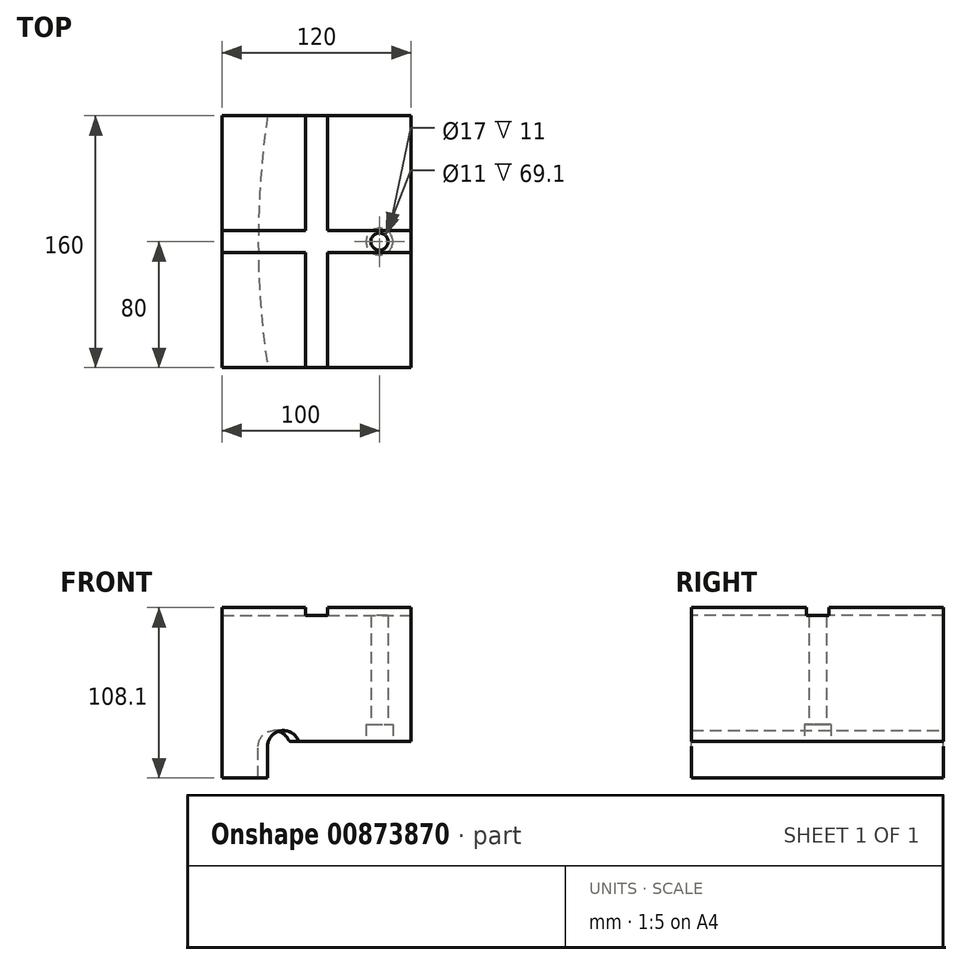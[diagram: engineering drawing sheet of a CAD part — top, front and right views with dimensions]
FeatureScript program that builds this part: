
annotation { "Feature Type Name" : "Feature", "Feature Type Description" : "" }
export const myFeature = defineFeature(function(context is Context, id is Id, definition is map)
    precondition{}
    {
        {
            var Q0;
            Q0=qCreatedBy(makeId("Front.planeOp"),FACE);
            var sketch = newSketch(context, id + "F0", { "sketchPlane" : qUnion([Q0])});
            skLineSegment(sketch, "E0", {"start": v(-542, 114.4) * mm, "end": v(-542, 136.4) * mm});
            skArc(sketch, "E1", {"start": v(-523.02, 140.8) * mm, "mid": v(-534.26, 146.14) * mm, "end": v(-542, 136.4) * mm});
            skLineSegment(sketch, "E2", {"start": v(-445, 139.4) * mm, "end": v(-520.78, 139.4) * mm});
            skPoint(sketch, "E3.visualSharp", {"position": v(-522.46, 139.4) * mm});
            skArc(sketch, "E3.filletArc", {"start": v(-523.02, 140.8) * mm, "mid": v(-522.1, 139.78) * mm, "end": v(-520.78, 139.4) * mm});
            skLineSegment(sketch, "E4", {"start": v(-542, 116.4) * mm, "end": v(-542, 114.4) * mm, "construction": true});
            skLineSegment(sketch, "E5", {"start": v(-445, 139.4) * mm, "end": v(-445, 224.5) * mm});
            skLineSegment(sketch, "E6", {"start": v(-445, 224.5) * mm, "end": v(-565, 224.5) * mm});
            skLineSegment(sketch, "E7", {"start": v(-565, 224.5) * mm, "end": v(-565, 116.4) * mm});
            skLineSegment(sketch, "E8", {"start": v(-565, 116.4) * mm, "end": v(-542, 116.4) * mm});
            skSolve(sketch);
        }
        {
            var Q0;
            Q0=qCreatedBy(makeId("Top.planeOp"),FACE);
            cPlane(context, id + "F1", {"entities" : qUnion([Q0]), "cplaneType" : CPlaneType.OFFSET, "offset" : 139.4 * mm, "width" : 150 * mm, "height" : 150 * mm});
        }
        {
            var Q0;
            Q0=qCreatedBy(id+"F1.planeOp",FACE);
            var sketch = newSketch(context, id + "F2", { "sketchPlane" : qUnion([Q0])});
            skArc(sketch, "E9", {"start": v(-340.89, 286.04) * mm, "mid": v(-445, 0) * mm, "end": v(-340.89, -286.04) * mm});
            skLineSegment(sketch, "E10", {"start": v(0, 0) * mm, "end": v(-340.89, 286.04) * mm, "construction": true});
            skLineSegment(sketch, "E11.MirrorCS", {"start": v(0, 0) * mm, "end": v(-340.89, -286.04) * mm, "construction": true});
            skSolve(sketch);
        }
        {
            var Q0;
            {var subQ0=sQuery(id+"F0.wireOp",EDGE,"E1");Q0=makeQuery(id+"F0.imprint","IMPRINT",FACE,{"disambiguationData":[TD([[makeQuery(id+"F0.imprint","IMPRINT",EDGE,{"derivedFrom":subQ0}),-1.0]])]});}
            var Q1;
            Q1=sQuery(id+"F2.wireOp",EDGE,"E9");
            sweep(context, id + "F3", {"profiles" : qUnion([Q0]), "path" : qUnion([Q1])});
        }
        {
            var Q0;
            Q0=makeQuery(id+"F3.opSweep","SWEPT_FACE",FACE,{"disambiguationData":[OSD([sQuery(id+"F0.wireOp",EDGE,"E6"),sQuery(id+"F2.wireOp",EDGE,"E9")])]});
            var sketch = newSketch(context, id + "F4", { "sketchPlane" : qUnion([Q0])});
            skLineSegment(sketch, "E12.bottom", {"start": v(-559.3, 80) * mm, "end": v(-445, 80) * mm});
            skLineSegment(sketch, "E12.top", {"start": v(-559.3, -80) * mm, "end": v(-445, -80) * mm});
            skLineSegment(sketch, "E12.right", {"start": v(-445, 80) * mm, "end": v(-445, -80) * mm});
            skLineSegment(sketch, "E13", {"start": v(0, 0) * mm, "end": v(-445, 0) * mm, "construction": true});
            skArc(sketch, "E14", {"start": v(-432.82, 363.17) * mm, "mid": v(-565, 0) * mm, "end": v(-432.82, -363.17) * mm});
            skArc(sketch, "E15", {"start": v(-340.89, 286.04) * mm, "mid": v(-445, 0) * mm, "end": v(-340.89, -286.04) * mm});
            skLineSegment(sketch, "E16", {"start": v(-432.82, 363.17) * mm, "end": v(0, 0) * mm, "construction": true});
            skLineSegment(sketch, "E17", {"start": v(-432.82, -363.17) * mm, "end": v(0, 0) * mm, "construction": true});
            skLineSegment(sketch, "E18", {"start": v(-432.82, -363.17) * mm, "end": v(-340.89, -286.04) * mm});
            skLineSegment(sketch, "E19", {"start": v(-432.82, 363.17) * mm, "end": v(-340.89, 286.04) * mm});
            skSolve(sketch);
        }
        {
            var Q0;
            {var subQ2=sQuery(id+"F4.wireOp",EDGE,"E12.bottom");Q0=makeQuery(id+"F4.imprint","IMPRINT",FACE,{"disambiguationData":[TD([[makeQuery(id+"F4.imprint","IMPRINT",EDGE,{"derivedFrom":subQ2}),1.0]])]});}
            var Q1;
            {var subQ4=sQuery(id+"F4.wireOp",EDGE,"E12.top");Q1=makeQuery(id+"F4.imprint","IMPRINT",FACE,{"disambiguationData":[TD([[makeQuery(id+"F4.imprint","IMPRINT",EDGE,{"derivedFrom":subQ4}),-1.0]])]});}
            extrude(context, id + "F5", {"entities" : qUnion([Q0, Q1]), "operationType" : NewBodyOperationType.REMOVE, "endBound" : BoundingType.UP_TO_NEXT, "oppositeDirection" : true, "depth" : 25 * mm, "offsetDistance" : 25 * mm});
        }
        {
            var Q0;
            Q0=makeQuery(id+"F3.opSweep","SWEPT_FACE",FACE,{"disambiguationData":[OSD([sQuery(id+"F0.wireOp",EDGE,"E6"),sQuery(id+"F2.wireOp",EDGE,"E9")])]});
            var sketch = newSketch(context, id + "F6", { "sketchPlane" : qUnion([Q0])});
            skLineSegment(sketch, "E20", {"start": v(-559.3, 80) * mm, "end": v(-565, 80) * mm});
            skLineSegment(sketch, "E21", {"start": v(-565, 80) * mm, "end": v(-565, -80) * mm});
            skLineSegment(sketch, "E22", {"start": v(-565, -80) * mm, "end": v(-559.3, -80) * mm});
            skArc(sketch, "E23", {"start": v(-559.3, 80) * mm, "mid": v(-565, 0) * mm, "end": v(-559.3, -80) * mm});
            skSolve(sketch);
        }
        {
            var Q0;
            Q0 = qSketchRegion(id + "F6", true);
            var Q1;
            Q1=makeQuery(id+"F3.opSweep","SWEPT_FACE",FACE,{"disambiguationData":[OSD([sQuery(id+"F0.wireOp",EDGE,"E8"),sQuery(id+"F2.wireOp",EDGE,"E9")])]});
            extrude(context, id + "F7", {"entities" : qUnion([Q0]), "operationType" : NewBodyOperationType.ADD, "endBound" : BoundingType.UP_TO_SURFACE, "oppositeDirection" : true, "depth" : 25 * mm, "endBoundEntityFace" : qUnion([Q1]), "offsetDistance" : 25 * mm});
        }
        {
            var Q0;
            {var subQ0=sQuery(id+"F6.wireOp",EDGE,"E23");var subQ1=sQuery(id+"F6.wireOp",EDGE,"E21");Q0=makeQuery(id+"F7.boolean.opBoolean","MERGE",FACE,{"derivedFrom":[makeQuery(id+"F3.opSweep","SWEPT_FACE",FACE,{"disambiguationData":[OSD([sQuery(id+"F0.wireOp",EDGE,"E6"),sQuery(id+"F2.wireOp",EDGE,"E9")])]}),makeQuery(id+"F7.opExtrude","CAP_FACE",FACE,{"disambiguationData":[OSD([sQuery(id+"F6.wireOp",EDGE,"E20"),subQ1,subQ0])],"isStart":true}),makeQuery(id+"F7.opExtrude","CAP_FACE",FACE,{"disambiguationData":[OSD([subQ1,sQuery(id+"F6.wireOp",EDGE,"E22"),subQ0])],"isStart":true})]});}
            var sketch = newSketch(context, id + "F8", { "sketchPlane" : qUnion([Q0])});
            skLineSegment(sketch, "E24.bottom", {"start": v(-512, 80) * mm, "end": v(-498, 80) * mm});
            skLineSegment(sketch, "E24.top", {"start": v(-512, -80) * mm, "end": v(-498, -80) * mm});
            skLineSegment(sketch, "E24.left", {"start": v(-512, 80) * mm, "end": v(-512, 7) * mm});
            skLineSegment(sketch, "E24.right", {"start": v(-498, 80) * mm, "end": v(-498, 7) * mm});
            skLineSegment(sketch, "E25.bottom", {"start": v(-565, 7) * mm, "end": v(-512, 7) * mm});
            skLineSegment(sketch, "E25.top", {"start": v(-565, -7) * mm, "end": v(-512, -7) * mm});
            skLineSegment(sketch, "E25.left", {"start": v(-565, 7) * mm, "end": v(-565, -7) * mm});
            skLineSegment(sketch, "E25.right", {"start": v(-445, 7) * mm, "end": v(-445, -7) * mm});
            skLineSegment(sketch, "E26.trimOffspring", {"start": v(-498, 7) * mm, "end": v(-445, 7) * mm});
            skLineSegment(sketch, "E27.trimOffspring", {"start": v(-512, -7) * mm, "end": v(-512, -80) * mm});
            skLineSegment(sketch, "E28.trimOffspring", {"start": v(-498, -7) * mm, "end": v(-445, -7) * mm});
            skLineSegment(sketch, "E29.trimOffspring", {"start": v(-498, -7) * mm, "end": v(-498, -80) * mm});
            skSolve(sketch);
        }
        {
            var Q0;
            Q0 = qSketchRegion(id + "F8", true);
            extrude(context, id + "F9", {"entities" : qUnion([Q0]), "operationType" : NewBodyOperationType.REMOVE, "oppositeDirection" : true, "depth" : 5 * mm, "offsetDistance" : 25 * mm});
        }
        {
            var Q0;
            Q0=makeQuery(id+"F3.opSweep","SWEPT_FACE",FACE,{"disambiguationData":[OSD([sQuery(id+"F0.wireOp",EDGE,"E2"),sQuery(id+"F2.wireOp",EDGE,"E9")])]});
            var sketch = newSketch(context, id + "F10", { "sketchPlane" : qUnion([Q0])});
            skCircle(sketch, "E30", {"center": v(-465, 0) * mm, "radius": 8.5 * mm});
            skSolve(sketch);
        }
        {
            var Q0;
            Q0=makeQuery(id+"F10.imprint","IMPRINT",FACE,{"disambiguationData":[TD([[makeQuery(id+"F10.imprint","IMPRINT",EDGE,{"derivedFrom":sQuery(id+"F10.wireOp",EDGE,"E30")}),1.0]])]});
            extrude(context, id + "F11", {"entities" : qUnion([Q0]), "operationType" : NewBodyOperationType.REMOVE, "oppositeDirection" : true, "depth" : 11 * mm, "offsetDistance" : 25 * mm});
        }
        {
            var Q0;
            Q0=makeQuery(id+"F11.boolean.opBoolean","COPY",FACE,{"derivedFrom":makeQuery(id+"F11.opExtrude","CAP_FACE",FACE,{"disambiguationData":[OSD([sQuery(id+"F10.wireOp",EDGE,"E30")])],"isStart":false})});
            var sketch = newSketch(context, id + "F12", { "sketchPlane" : qUnion([Q0])});
            skCircle(sketch, "E31", {"center": v(-465, 0) * mm, "radius": 5.5 * mm});
            skSolve(sketch);
        }
        {
            var Q0;
            Q0=makeQuery(id+"F12.imprint","IMPRINT",FACE,{"disambiguationData":[TD([[makeQuery(id+"F12.imprint","IMPRINT",EDGE,{"derivedFrom":sQuery(id+"F12.wireOp",EDGE,"E31")}),1.0]])]});
            var Q1;
            Q1=makeQuery(id+"F9.boolean.opBoolean","COPY",FACE,{"derivedFrom":makeQuery(id+"F9.opExtrude","CAP_FACE",FACE,{"disambiguationData":[OSD([sQuery(id+"F8.wireOp",EDGE,"E24.bottom"),sQuery(id+"F8.wireOp",EDGE,"E24.top"),sQuery(id+"F8.wireOp",EDGE,"E24.left"),sQuery(id+"F8.wireOp",EDGE,"E24.right"),sQuery(id+"F8.wireOp",EDGE,"E25.bottom"),sQuery(id+"F8.wireOp",EDGE,"E25.top"),sQuery(id+"F8.wireOp",EDGE,"E25.left"),sQuery(id+"F8.wireOp",EDGE,"E25.right"),sQuery(id+"F8.wireOp",EDGE,"E26.trimOffspring"),sQuery(id+"F8.wireOp",EDGE,"E27.trimOffspring"),sQuery(id+"F8.wireOp",EDGE,"E28.trimOffspring"),sQuery(id+"F8.wireOp",EDGE,"E29.trimOffspring")])],"isStart":false})});
            extrude(context, id + "F13", {"entities" : qUnion([Q0]), "operationType" : NewBodyOperationType.REMOVE, "endBound" : BoundingType.UP_TO_SURFACE, "oppositeDirection" : true, "depth" : 25 * mm, "endBoundEntityFace" : qUnion([Q1]), "offsetDistance" : 25 * mm});
        }
    });
